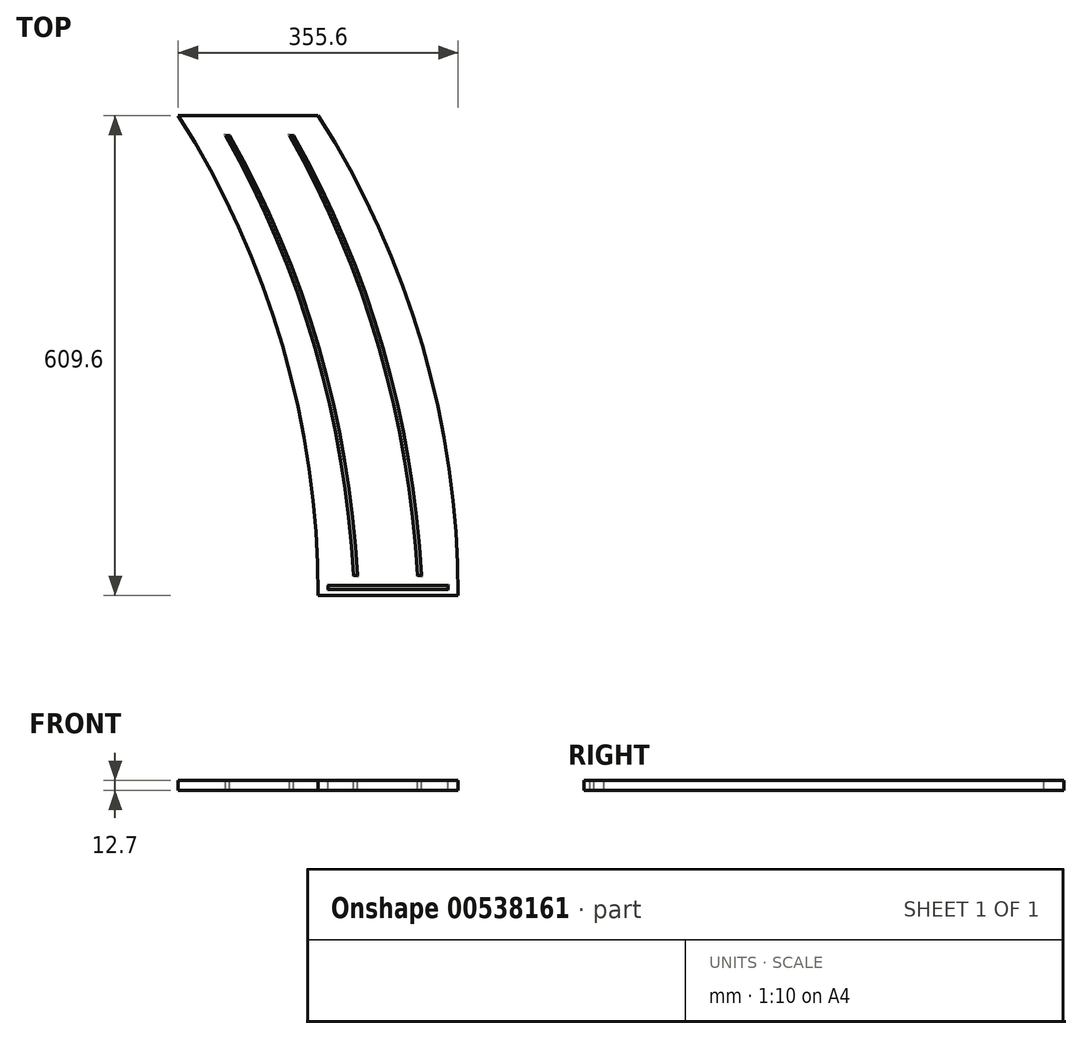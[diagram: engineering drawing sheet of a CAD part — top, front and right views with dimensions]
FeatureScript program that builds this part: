
annotation { "Feature Type Name" : "Feature", "Feature Type Description" : "" }
export const myFeature = defineFeature(function(context is Context, id is Id, definition is map)
    precondition{}
    {
        {
            var Q0;
            Q0=qCreatedBy(makeId("Top.planeOp"),FACE);
            var sketch = newSketch(context, id + "F0", { "sketchPlane" : qUnion([Q0])});
            skLineSegment(sketch, "E0", {"start": v(0, 0) * mm, "end": v(177.8, 0) * mm});
            skLineSegment(sketch, "E1", {"start": v(0, 609.6) * mm, "end": v(-177.8, 609.6) * mm});
            skArc(sketch, "E2", {"start": v(0, 0) * mm, "mid": v(-45.36, 317.5) * mm, "end": v(-177.8, 609.6) * mm});
            skArc(sketch, "E3", {"start": v(177.8, 0) * mm, "mid": v(132.44, 317.5) * mm, "end": v(0, 609.6) * mm});
            skSolve(sketch);
        }
        {
            var Q0;
            Q0=makeQuery(id+"F0.imprint","IMPRINT",FACE,{"disambiguationData":[TD([[makeQuery(id+"F0.imprint","IMPRINT",EDGE,{"derivedFrom":sQuery(id+"F0.wireOp",EDGE,"E0")}),1.0]])]});
            extrude(context, id + "F1", {"entities" : qUnion([Q0]), "depth" : 12.7 * mm, "offsetDistance" : 25.4 * mm});
        }
        {
            var Q0;
            Q0=makeQuery(id+"F1.opExtrude","CAP_FACE",FACE,{"disambiguationData":[OSD([sQuery(id+"F0.wireOp",EDGE,"E0"),sQuery(id+"F0.wireOp",EDGE,"E1"),sQuery(id+"F0.wireOp",EDGE,"E2"),sQuery(id+"F0.wireOp",EDGE,"E3")])],"isStart":false});
            var sketch = newSketch(context, id + "F2", { "sketchPlane" : qUnion([Q0])});
            skArc(sketch, "E4", {"start": v(49.75, 25.4) * mm, "mid": v(1.16, 314.2) * mm, "end": v(-112.3, 584.2) * mm});
            skArc(sketch, "E5", {"start": v(44.67, 25.4) * mm, "mid": v(-3.92, 314.2) * mm, "end": v(-117.37, 584.2) * mm});
            skLineSegment(sketch, "E6", {"start": v(44.67, 25.4) * mm, "end": v(49.75, 25.4) * mm});
            skLineSegment(sketch, "E7", {"start": v(-117.37, 584.2) * mm, "end": v(-112.3, 584.2) * mm});
            skSolve(sketch);
        }
        {
            var Q0;
            Q0=makeQuery(id+"F2.imprint","IMPRINT",FACE,{"disambiguationData":[TD([[makeQuery(id+"F2.imprint","IMPRINT",EDGE,{"derivedFrom":sQuery(id+"F2.wireOp",EDGE,"E4")}),1.0]])]});
            extrude(context, id + "F3", {"entities" : qUnion([Q0]), "operationType" : NewBodyOperationType.REMOVE, "endBound" : BoundingType.THROUGH_ALL, "oppositeDirection" : true, "depth" : 25.4 * mm, "offsetDistance" : 25.4 * mm});
        }
        {
            var Q0;
            Q0=makeQuery(id+"F1.opExtrude","CAP_FACE",FACE,{"disambiguationData":[OSD([sQuery(id+"F0.wireOp",EDGE,"E0"),sQuery(id+"F0.wireOp",EDGE,"E1"),sQuery(id+"F0.wireOp",EDGE,"E2"),sQuery(id+"F0.wireOp",EDGE,"E3")])],"isStart":false});
            var sketch = newSketch(context, id + "F4", { "sketchPlane" : qUnion([Q0])});
            skArc(sketch, "E8", {"start": v(125.95, 25.4) * mm, "mid": v(77.36, 314.2) * mm, "end": v(-36.1, 584.2) * mm});
            skArc(sketch, "E9", {"start": v(131.03, 25.4) * mm, "mid": v(82.44, 314.2) * mm, "end": v(-31.01, 584.2) * mm});
            skLineSegment(sketch, "E10", {"start": v(125.95, 25.4) * mm, "end": v(131.03, 25.4) * mm});
            skLineSegment(sketch, "E11", {"start": v(-31.01, 584.2) * mm, "end": v(-36.1, 584.2) * mm});
            skSolve(sketch);
        }
        {
            var Q0;
            Q0=makeQuery(id+"F4.imprint","IMPRINT",FACE,{"disambiguationData":[TD([[makeQuery(id+"F4.imprint","IMPRINT",EDGE,{"derivedFrom":sQuery(id+"F4.wireOp",EDGE,"E8")}),-1.0]])]});
            extrude(context, id + "F5", {"entities" : qUnion([Q0]), "operationType" : NewBodyOperationType.REMOVE, "endBound" : BoundingType.THROUGH_ALL, "oppositeDirection" : true, "depth" : 25.4 * mm, "offsetDistance" : 25.4 * mm});
        }
        {
            var Q0;
            Q0=makeQuery(id+"F1.opExtrude","CAP_FACE",FACE,{"disambiguationData":[OSD([sQuery(id+"F0.wireOp",EDGE,"E0"),sQuery(id+"F0.wireOp",EDGE,"E1"),sQuery(id+"F0.wireOp",EDGE,"E2"),sQuery(id+"F0.wireOp",EDGE,"E3")])],"isStart":false});
            var sketch = newSketch(context, id + "F6", { "sketchPlane" : qUnion([Q0])});
            skLineSegment(sketch, "E12", {"start": v(165.1, 12.7) * mm, "end": v(12.7, 12.7) * mm});
            skLineSegment(sketch, "E13", {"start": v(165.1, 12.7) * mm, "end": v(165.1, 7.62) * mm});
            skPoint(sketch, "E13.endSnap0", {"position": v(165.1, 6.35) * mm});
            skLineSegment(sketch, "E14", {"start": v(165.1, 7.62) * mm, "end": v(12.7, 7.62) * mm});
            skLineSegment(sketch, "E15", {"start": v(12.7, 7.62) * mm, "end": v(12.7, 12.7) * mm});
            skSolve(sketch);
        }
        {
            var Q0;
            Q0=makeQuery(id+"F6.imprint","IMPRINT",FACE,{"disambiguationData":[TD([[makeQuery(id+"F6.imprint","IMPRINT",EDGE,{"derivedFrom":sQuery(id+"F6.wireOp",EDGE,"E12")}),1.0]])]});
            extrude(context, id + "F7", {"entities" : qUnion([Q0]), "operationType" : NewBodyOperationType.REMOVE, "endBound" : BoundingType.THROUGH_ALL, "oppositeDirection" : true, "depth" : 25.4 * mm, "offsetDistance" : 25.4 * mm});
        }
        {
            var Q0;
            Q0=makeQuery(id+"F3.boolean.opBoolean","COPY",EDGE,{"derivedFrom":makeQuery(id+"F3.opExtrude","CAP_EDGE",EDGE,{"disambiguationData":[OSD([sQuery(id+"F2.wireOp",EDGE,"E7")])],"isStart":true})});
            var Q1;
            Q1=makeQuery(id+"F3.boolean.opBoolean","COPY",EDGE,{"derivedFrom":makeQuery(id+"F3.opExtrude","CAP_EDGE",EDGE,{"disambiguationData":[OSD([sQuery(id+"F2.wireOp",EDGE,"E4")])],"isStart":true})});
            var Q2;
            Q2=makeQuery(id+"F3.boolean.opBoolean","COPY",EDGE,{"derivedFrom":makeQuery(id+"F3.opExtrude","CAP_EDGE",EDGE,{"disambiguationData":[OSD([sQuery(id+"F2.wireOp",EDGE,"E5")])],"isStart":true})});
            var Q3;
            Q3=makeQuery(id+"F3.boolean.opBoolean","COPY",EDGE,{"derivedFrom":makeQuery(id+"F3.opExtrude","CAP_EDGE",EDGE,{"disambiguationData":[OSD([sQuery(id+"F2.wireOp",EDGE,"E6")])],"isStart":true})});
            var Q4;
            Q4=makeQuery(id+"F7.boolean.opBoolean","COPY",EDGE,{"derivedFrom":makeQuery(id+"F7.opExtrude","CAP_EDGE",EDGE,{"disambiguationData":[OSD([sQuery(id+"F6.wireOp",EDGE,"E12")])],"isStart":true})});
            var Q5;
            Q5=makeQuery(id+"F7.boolean.opBoolean","COPY",EDGE,{"derivedFrom":makeQuery(id+"F7.opExtrude","CAP_EDGE",EDGE,{"disambiguationData":[OSD([sQuery(id+"F6.wireOp",EDGE,"E15")])],"isStart":true})});
            var Q6;
            Q6=makeQuery(id+"F7.boolean.opBoolean","COPY",EDGE,{"derivedFrom":makeQuery(id+"F7.opExtrude","CAP_EDGE",EDGE,{"disambiguationData":[OSD([sQuery(id+"F6.wireOp",EDGE,"E14")])],"isStart":true})});
            var Q7;
            Q7=makeQuery(id+"F7.boolean.opBoolean","COPY",EDGE,{"derivedFrom":makeQuery(id+"F7.opExtrude","CAP_EDGE",EDGE,{"disambiguationData":[OSD([sQuery(id+"F6.wireOp",EDGE,"E13")])],"isStart":true})});
            var Q8;
            Q8=makeQuery(id+"F5.boolean.opBoolean","COPY",EDGE,{"derivedFrom":makeQuery(id+"F5.opExtrude","CAP_EDGE",EDGE,{"disambiguationData":[OSD([sQuery(id+"F4.wireOp",EDGE,"E9")])],"isStart":true})});
            var Q9;
            Q9=makeQuery(id+"F5.boolean.opBoolean","COPY",EDGE,{"derivedFrom":makeQuery(id+"F5.opExtrude","CAP_EDGE",EDGE,{"disambiguationData":[OSD([sQuery(id+"F4.wireOp",EDGE,"E8")])],"isStart":true})});
            var Q10;
            Q10=makeQuery(id+"F5.boolean.opBoolean","COPY",EDGE,{"derivedFrom":makeQuery(id+"F5.opExtrude","CAP_EDGE",EDGE,{"disambiguationData":[OSD([sQuery(id+"F4.wireOp",EDGE,"E10")])],"isStart":true})});
            var Q11;
            Q11=makeQuery(id+"F5.boolean.opBoolean","COPY",EDGE,{"derivedFrom":makeQuery(id+"F5.opExtrude","CAP_EDGE",EDGE,{"disambiguationData":[OSD([sQuery(id+"F4.wireOp",EDGE,"E11")])],"isStart":true})});
            var Q12;
            Q12=makeQuery(id+"F3.boolean.opBoolean","INTERSECT",EDGE,{"derivedFrom":[makeQuery(id+"F1.opExtrude","CAP_FACE",FACE,{"disambiguationData":[OSD([sQuery(id+"F0.wireOp",EDGE,"E0"),sQuery(id+"F0.wireOp",EDGE,"E1"),sQuery(id+"F0.wireOp",EDGE,"E2"),sQuery(id+"F0.wireOp",EDGE,"E3")])],"isStart":true}),makeQuery(id+"F3.opExtrude","SWEPT_FACE",FACE,{"disambiguationData":[OSD([sQuery(id+"F2.wireOp",EDGE,"E7")])]})]});
            var Q13;
            Q13=makeQuery(id+"F3.boolean.opBoolean","INTERSECT",EDGE,{"derivedFrom":[makeQuery(id+"F1.opExtrude","CAP_FACE",FACE,{"disambiguationData":[OSD([sQuery(id+"F0.wireOp",EDGE,"E0"),sQuery(id+"F0.wireOp",EDGE,"E1"),sQuery(id+"F0.wireOp",EDGE,"E2"),sQuery(id+"F0.wireOp",EDGE,"E3")])],"isStart":true}),makeQuery(id+"F3.opExtrude","SWEPT_FACE",FACE,{"disambiguationData":[OSD([sQuery(id+"F2.wireOp",EDGE,"E4")])]})]});
            var Q14;
            Q14=makeQuery(id+"F3.boolean.opBoolean","INTERSECT",EDGE,{"derivedFrom":[makeQuery(id+"F1.opExtrude","CAP_FACE",FACE,{"disambiguationData":[OSD([sQuery(id+"F0.wireOp",EDGE,"E0"),sQuery(id+"F0.wireOp",EDGE,"E1"),sQuery(id+"F0.wireOp",EDGE,"E2"),sQuery(id+"F0.wireOp",EDGE,"E3")])],"isStart":true}),makeQuery(id+"F3.opExtrude","SWEPT_FACE",FACE,{"disambiguationData":[OSD([sQuery(id+"F2.wireOp",EDGE,"E5")])]})]});
            var Q15;
            Q15=makeQuery(id+"F3.boolean.opBoolean","INTERSECT",EDGE,{"derivedFrom":[makeQuery(id+"F1.opExtrude","CAP_FACE",FACE,{"disambiguationData":[OSD([sQuery(id+"F0.wireOp",EDGE,"E0"),sQuery(id+"F0.wireOp",EDGE,"E1"),sQuery(id+"F0.wireOp",EDGE,"E2"),sQuery(id+"F0.wireOp",EDGE,"E3")])],"isStart":true}),makeQuery(id+"F3.opExtrude","SWEPT_FACE",FACE,{"disambiguationData":[OSD([sQuery(id+"F2.wireOp",EDGE,"E6")])]})]});
            var Q16;
            Q16=makeQuery(id+"F5.boolean.opBoolean","INTERSECT",EDGE,{"derivedFrom":[makeQuery(id+"F1.opExtrude","CAP_FACE",FACE,{"disambiguationData":[OSD([sQuery(id+"F0.wireOp",EDGE,"E0"),sQuery(id+"F0.wireOp",EDGE,"E1"),sQuery(id+"F0.wireOp",EDGE,"E2"),sQuery(id+"F0.wireOp",EDGE,"E3")])],"isStart":true}),makeQuery(id+"F5.opExtrude","SWEPT_FACE",FACE,{"disambiguationData":[OSD([sQuery(id+"F4.wireOp",EDGE,"E10")])]})]});
            var Q17;
            Q17=makeQuery(id+"F5.boolean.opBoolean","INTERSECT",EDGE,{"derivedFrom":[makeQuery(id+"F1.opExtrude","CAP_FACE",FACE,{"disambiguationData":[OSD([sQuery(id+"F0.wireOp",EDGE,"E0"),sQuery(id+"F0.wireOp",EDGE,"E1"),sQuery(id+"F0.wireOp",EDGE,"E2"),sQuery(id+"F0.wireOp",EDGE,"E3")])],"isStart":true}),makeQuery(id+"F5.opExtrude","SWEPT_FACE",FACE,{"disambiguationData":[OSD([sQuery(id+"F4.wireOp",EDGE,"E9")])]})]});
            var Q18;
            Q18=makeQuery(id+"F5.boolean.opBoolean","INTERSECT",EDGE,{"derivedFrom":[makeQuery(id+"F1.opExtrude","CAP_FACE",FACE,{"disambiguationData":[OSD([sQuery(id+"F0.wireOp",EDGE,"E0"),sQuery(id+"F0.wireOp",EDGE,"E1"),sQuery(id+"F0.wireOp",EDGE,"E2"),sQuery(id+"F0.wireOp",EDGE,"E3")])],"isStart":true}),makeQuery(id+"F5.opExtrude","SWEPT_FACE",FACE,{"disambiguationData":[OSD([sQuery(id+"F4.wireOp",EDGE,"E8")])]})]});
            var Q19;
            Q19=makeQuery(id+"F5.boolean.opBoolean","INTERSECT",EDGE,{"derivedFrom":[makeQuery(id+"F1.opExtrude","CAP_FACE",FACE,{"disambiguationData":[OSD([sQuery(id+"F0.wireOp",EDGE,"E0"),sQuery(id+"F0.wireOp",EDGE,"E1"),sQuery(id+"F0.wireOp",EDGE,"E2"),sQuery(id+"F0.wireOp",EDGE,"E3")])],"isStart":true}),makeQuery(id+"F5.opExtrude","SWEPT_FACE",FACE,{"disambiguationData":[OSD([sQuery(id+"F4.wireOp",EDGE,"E11")])]})]});
            var Q20;
            Q20=makeQuery(id+"F7.boolean.opBoolean","INTERSECT",EDGE,{"derivedFrom":[makeQuery(id+"F1.opExtrude","CAP_FACE",FACE,{"disambiguationData":[OSD([sQuery(id+"F0.wireOp",EDGE,"E0"),sQuery(id+"F0.wireOp",EDGE,"E1"),sQuery(id+"F0.wireOp",EDGE,"E2"),sQuery(id+"F0.wireOp",EDGE,"E3")])],"isStart":true}),makeQuery(id+"F7.opExtrude","SWEPT_FACE",FACE,{"disambiguationData":[OSD([sQuery(id+"F6.wireOp",EDGE,"E15")])]})]});
            var Q21;
            Q21=makeQuery(id+"F7.boolean.opBoolean","INTERSECT",EDGE,{"derivedFrom":[makeQuery(id+"F1.opExtrude","CAP_FACE",FACE,{"disambiguationData":[OSD([sQuery(id+"F0.wireOp",EDGE,"E0"),sQuery(id+"F0.wireOp",EDGE,"E1"),sQuery(id+"F0.wireOp",EDGE,"E2"),sQuery(id+"F0.wireOp",EDGE,"E3")])],"isStart":true}),makeQuery(id+"F7.opExtrude","SWEPT_FACE",FACE,{"disambiguationData":[OSD([sQuery(id+"F6.wireOp",EDGE,"E12")])]})]});
            var Q22;
            Q22=makeQuery(id+"F7.boolean.opBoolean","INTERSECT",EDGE,{"derivedFrom":[makeQuery(id+"F1.opExtrude","CAP_FACE",FACE,{"disambiguationData":[OSD([sQuery(id+"F0.wireOp",EDGE,"E0"),sQuery(id+"F0.wireOp",EDGE,"E1"),sQuery(id+"F0.wireOp",EDGE,"E2"),sQuery(id+"F0.wireOp",EDGE,"E3")])],"isStart":true}),makeQuery(id+"F7.opExtrude","SWEPT_FACE",FACE,{"disambiguationData":[OSD([sQuery(id+"F6.wireOp",EDGE,"E14")])]})]});
            var Q23;
            Q23=makeQuery(id+"F7.boolean.opBoolean","INTERSECT",EDGE,{"derivedFrom":[makeQuery(id+"F1.opExtrude","CAP_FACE",FACE,{"disambiguationData":[OSD([sQuery(id+"F0.wireOp",EDGE,"E0"),sQuery(id+"F0.wireOp",EDGE,"E1"),sQuery(id+"F0.wireOp",EDGE,"E2"),sQuery(id+"F0.wireOp",EDGE,"E3")])],"isStart":true}),makeQuery(id+"F7.opExtrude","SWEPT_FACE",FACE,{"disambiguationData":[OSD([sQuery(id+"F6.wireOp",EDGE,"E13")])]})]});
            fillet(context, id + "F8", {"entities" : qUnion([Q0, Q1, Q2, Q3, Q4, Q5, Q6, Q7, Q8, Q9, Q10, Q11, Q12, Q13, Q14, Q15, Q16, Q17, Q18, Q19, Q20, Q21, Q22, Q23]), "radius" : 1.27 * mm, "tangentPropagation" : true, "allowEdgeOverflow" : false});
        }
    });
